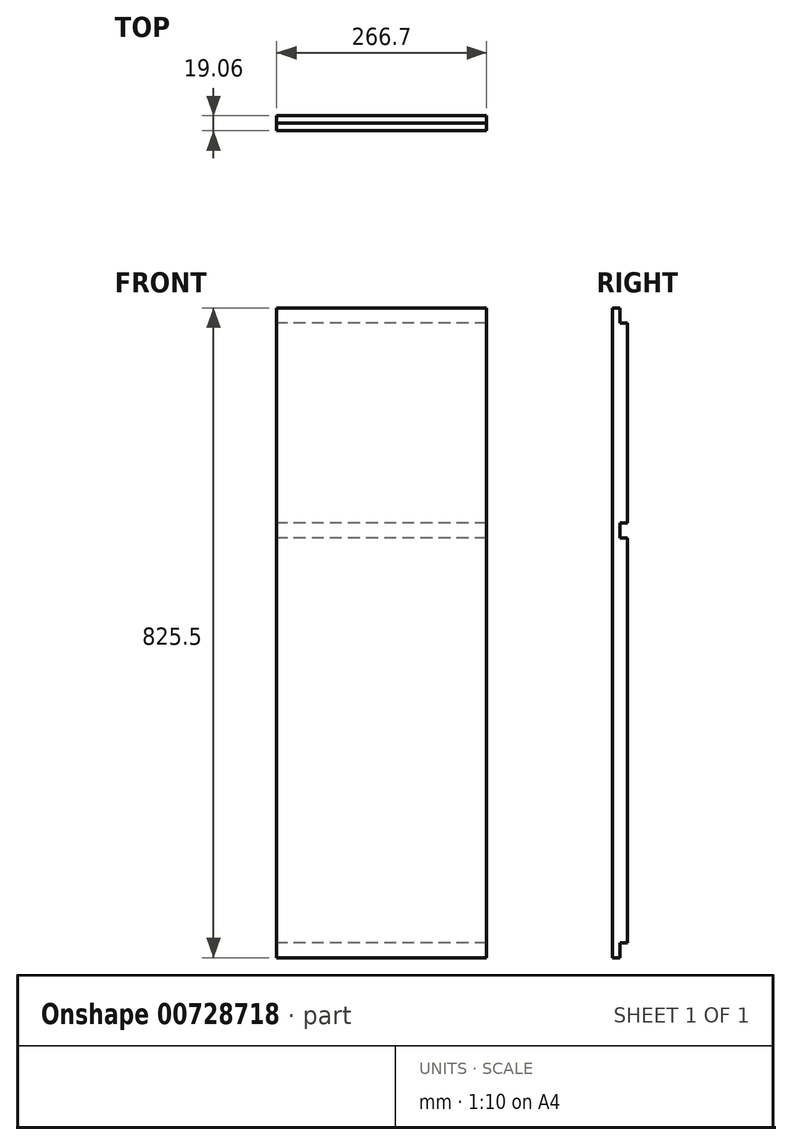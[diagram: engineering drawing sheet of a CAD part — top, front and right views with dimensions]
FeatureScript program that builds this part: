
annotation { "Feature Type Name" : "Feature", "Feature Type Description" : "" }
export const myFeature = defineFeature(function(context is Context, id is Id, definition is map)
    precondition{}
    {
        {
            var Q0;
            Q0=qCreatedBy(makeId("Right.planeOp"),FACE);
            var sketch = newSketch(context, id + "F0", { "sketchPlane" : qUnion([Q0])});
            skLineSegment(sketch, "E0.bottom", {"start": v(0, 412.75) * mm, "end": v(-9.53, 412.75) * mm});
            skLineSegment(sketch, "E0.top", {"start": v(0, -412.75) * mm, "end": v(-9.52, -412.75) * mm});
            skLineSegment(sketch, "E0.left", {"start": v(9.52, 393.7) * mm, "end": v(9.53, 139.7) * mm});
            skLineSegment(sketch, "E0.right", {"start": v(-9.53, 412.75) * mm, "end": v(-9.52, -412.75) * mm});
            skPoint(sketch, "E0.middle", {"position": v(0, 0) * mm});
            skPoint(sketch, "E1.oppositeSnap0", {"position": v(0, 412.75) * mm});
            skLineSegment(sketch, "E1.top", {"start": v(9.52, 393.7) * mm, "end": v(0, 393.7) * mm});
            skLineSegment(sketch, "E1.right", {"start": v(0, 412.75) * mm, "end": v(0, 393.7) * mm});
            skPoint(sketch, "E2.orphan", {"position": v(9.52, 412.75) * mm});
            skLineSegment(sketch, "E3.top", {"start": v(9.52, -393.7) * mm, "end": v(0, -393.7) * mm});
            skLineSegment(sketch, "E3.right", {"start": v(0, -412.75) * mm, "end": v(0, -393.7) * mm});
            skPoint(sketch, "E4.orphan", {"position": v(9.53, -412.75) * mm});
            skLineSegment(sketch, "E5.bottom", {"start": v(9.53, 139.7) * mm, "end": v(0, 139.7) * mm});
            skLineSegment(sketch, "E5.top", {"start": v(9.52, 120.65) * mm, "end": v(0, 120.65) * mm});
            skLineSegment(sketch, "E5.right", {"start": v(0, 139.7) * mm, "end": v(0, 120.65) * mm});
            skLineSegment(sketch, "E6.trimOffspring", {"start": v(9.53, 120.65) * mm, "end": v(9.53, -393.7) * mm});
            skSolve(sketch);
        }
        {
            var Q0;
            Q0 = qSketchRegion(id + "F0", true);
            extrude(context, id + "F1", {"entities" : qUnion([Q0]), "depth" : 266.7 * mm, "offsetDistance" : 25.4 * mm});
        }
    });
